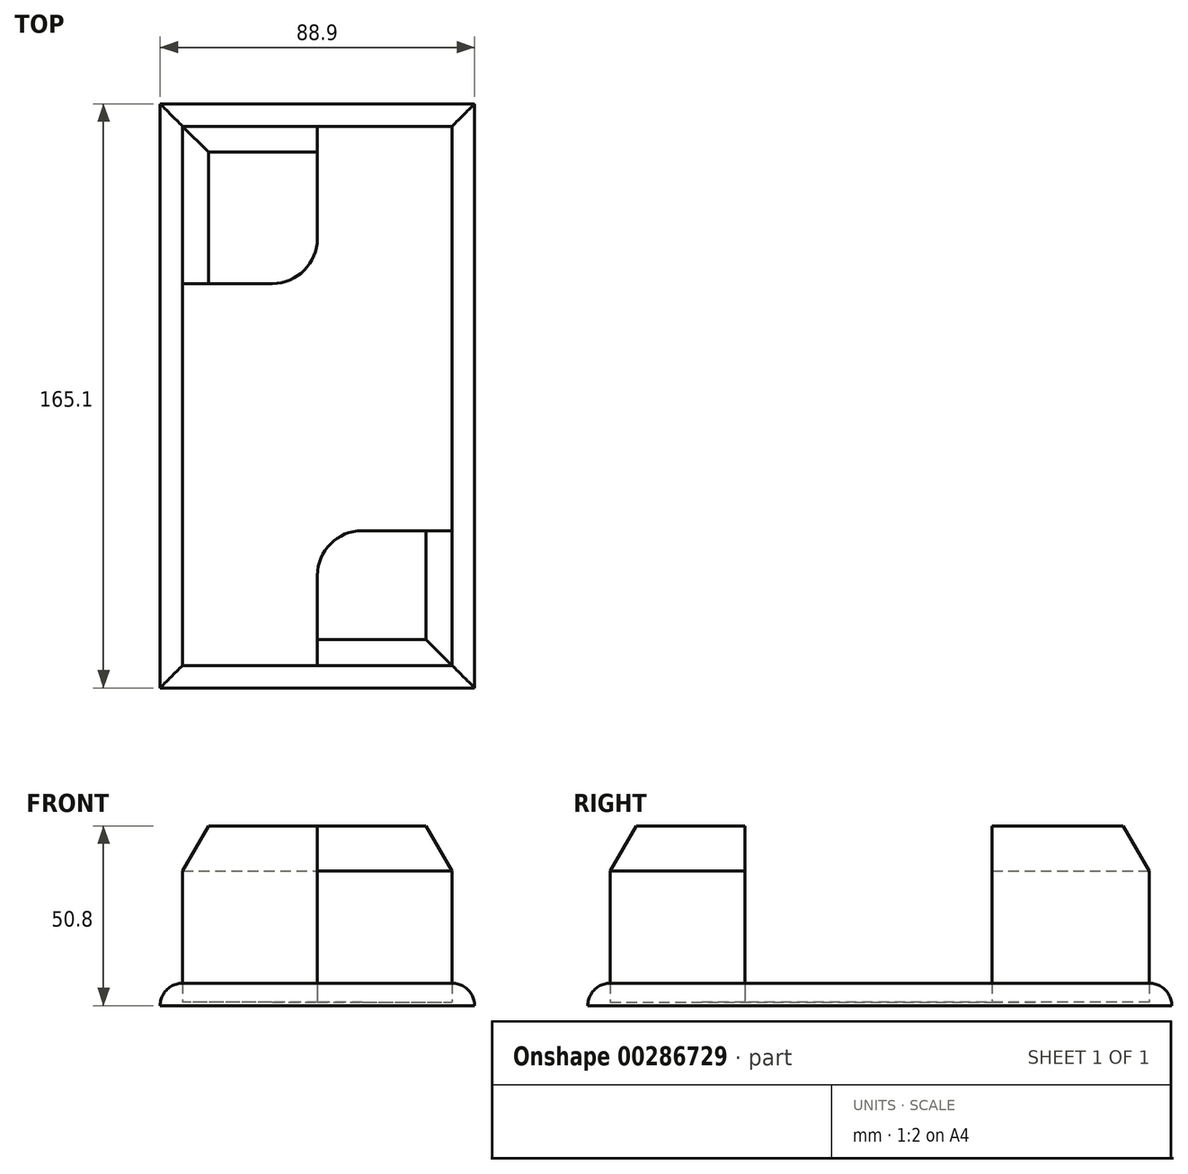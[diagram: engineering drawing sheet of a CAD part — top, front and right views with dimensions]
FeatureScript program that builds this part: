
annotation { "Feature Type Name" : "Feature", "Feature Type Description" : "" }
export const myFeature = defineFeature(function(context is Context, id is Id, definition is map)
    precondition{}
    {
        {
            var Q0;
            Q0=qCreatedBy(makeId("Top.planeOp"),FACE);
            var sketch = newSketch(context, id + "F0", { "sketchPlane" : qUnion([Q0])});
            skLineSegment(sketch, "E0", {"start": v(-50.93, 51.87) * mm, "end": v(25.27, 51.87) * mm});
            skLineSegment(sketch, "E1", {"start": v(25.27, 51.87) * mm, "end": v(25.27, -100.53) * mm});
            skLineSegment(sketch, "E2", {"start": v(25.27, -100.53) * mm, "end": v(-50.93, -100.53) * mm});
            skLineSegment(sketch, "E3", {"start": v(-50.93, -100.53) * mm, "end": v(-50.93, 51.87) * mm});
            skLineSegment(sketch, "E4.0", {"start": v(-57.28, 58.22) * mm, "end": v(31.62, 58.22) * mm});
            skLineSegment(sketch, "E4.1", {"start": v(-57.28, -106.88) * mm, "end": v(-57.28, 58.22) * mm});
            skLineSegment(sketch, "E4.2", {"start": v(31.62, -106.88) * mm, "end": v(-57.28, -106.88) * mm});
            skLineSegment(sketch, "E4.3", {"start": v(31.62, 58.22) * mm, "end": v(31.62, -106.88) * mm});
            skLineSegment(sketch, "E5", {"start": v(-12.83, 51.87) * mm, "end": v(-12.83, 20.12) * mm});
            skLineSegment(sketch, "E6", {"start": v(-25.53, 7.42) * mm, "end": v(-50.93, 7.42) * mm});
            skArc(sketch, "E7.filletArc", {"start": v(-25.53, 7.42) * mm, "mid": v(-16.55, 11.14) * mm, "end": v(-12.83, 20.12) * mm});
            skLineSegment(sketch, "E8", {"start": v(-12.83, -100.53) * mm, "end": v(-12.83, -75.13) * mm});
            skLineSegment(sketch, "E9", {"start": v(-0.13, -62.43) * mm, "end": v(25.27, -62.43) * mm});
            skArc(sketch, "E10.filletArc", {"start": v(-0.13, -62.43) * mm, "mid": v(-9.11, -66.15) * mm, "end": v(-12.83, -75.13) * mm});
            skSolve(sketch);
        }
        {
            var Q0;
            {var subQ9=sQuery(id+"F0.wireOp",EDGE,"E5");Q0=makeQuery(id+"F0.imprint","IMPRINT",FACE,{"disambiguationData":[TD([[makeQuery(id+"F0.imprint","IMPRINT",EDGE,{"derivedFrom":subQ9}),1.0]])]});}
            extrude(context, id + "F1", {"entities" : qUnion([Q0]), "depth" : mm});
        }
        {
            var Q0;
            {var subQ1=sQuery(id+"F0.wireOp",EDGE,"E8");Q0=makeQuery(id+"F0.imprint","IMPRINT",FACE,{"disambiguationData":[TD([[makeQuery(id+"F0.imprint","IMPRINT",EDGE,{"derivedFrom":subQ1}),-1.0]])]});}
            var Q1;
            {var subQ1=sQuery(id+"F0.wireOp",EDGE,"E5");Q1=makeQuery(id+"F0.imprint","IMPRINT",FACE,{"disambiguationData":[TD([[makeQuery(id+"F0.imprint","IMPRINT",EDGE,{"derivedFrom":subQ1}),-1.0]])]});}
            extrude(context, id + "F2", {"entities" : qUnion([Q0, Q1]), "operationType" : NewBodyOperationType.ADD, "depth" : 50.8 * mm});
        }
        {
            var Q0;
            Q0=makeQuery(id+"F0.imprint","IMPRINT",FACE,{"disambiguationData":[TD([[makeQuery(id+"F0.imprint","IMPRINT",EDGE,{"derivedFrom":sQuery(id+"F0.wireOp",EDGE,"E4.0")}),-1.0]])]});
            extrude(context, id + "F3", {"entities" : qUnion([Q0]), "operationType" : NewBodyOperationType.ADD, "depth" : 6.35 * mm});
        }
        {
            var Q0;
            Q0=makeQuery(id+"F3.opExtrude","CAP_EDGE",EDGE,{"disambiguationData":[OSD([sQuery(id+"F0.wireOp",EDGE,"E4.1")])],"isStart":false});
            var Q1;
            Q1=makeQuery(id+"F3.opExtrude","CAP_EDGE",EDGE,{"disambiguationData":[OSD([sQuery(id+"F0.wireOp",EDGE,"E4.2")])],"isStart":false});
            var Q2;
            Q2=makeQuery(id+"F3.opExtrude","CAP_EDGE",EDGE,{"disambiguationData":[OSD([sQuery(id+"F0.wireOp",EDGE,"E4.3")])],"isStart":false});
            var Q3;
            Q3=makeQuery(id+"F3.opExtrude","CAP_EDGE",EDGE,{"disambiguationData":[OSD([sQuery(id+"F0.wireOp",EDGE,"E4.0")])],"isStart":false});
            fillet(context, id + "F4", {"entities" : qUnion([Q0, Q1, Q2, Q3]), "radius" : 6.35 * mm, "tangentPropagation" : true, "allowEdgeOverflow" : false});
        }
        {
            var Q0;
            Q0=makeQuery(id+"F1.opExtrude","CAP_EDGE",EDGE,{"disambiguationData":[OSD([sQuery(id+"F0.wireOp",EDGE,"E1")])],"isStart":false});
            var Q1;
            Q1=makeQuery(id+"F1.opExtrude","CAP_EDGE",EDGE,{"disambiguationData":[OSD([sQuery(id+"F0.wireOp",EDGE,"E0")])],"isStart":false});
            var Q2;
            Q2=makeQuery(id+"F2.opExtrude","CAP_EDGE",EDGE,{"disambiguationData":[OSD([sQuery(id+"F0.wireOp",EDGE,"E0")])],"isStart":false});
            var Q3;
            Q3=makeQuery(id+"F2.opExtrude","CAP_EDGE",EDGE,{"disambiguationData":[OSD([sQuery(id+"F0.wireOp",EDGE,"E3")])],"isStart":false});
            var Q4;
            Q4=makeQuery(id+"F1.opExtrude","CAP_EDGE",EDGE,{"disambiguationData":[OSD([sQuery(id+"F0.wireOp",EDGE,"E3")])],"isStart":false});
            var Q5;
            Q5=makeQuery(id+"F2.opExtrude","CAP_EDGE",EDGE,{"disambiguationData":[OSD([sQuery(id+"F0.wireOp",EDGE,"E1")])],"isStart":false});
            var Q6;
            Q6=makeQuery(id+"F1.opExtrude","CAP_EDGE",EDGE,{"disambiguationData":[OSD([sQuery(id+"F0.wireOp",EDGE,"E2")])],"isStart":false});
            var Q7;
            Q7=makeQuery(id+"F2.opExtrude","CAP_EDGE",EDGE,{"disambiguationData":[OSD([sQuery(id+"F0.wireOp",EDGE,"E2")])],"isStart":false});
            chamfer(context, id + "F5", {"entities" : qUnion([Q0, Q1, Q2, Q3, Q4, Q5, Q6, Q7]), "chamferType" : ChamferType.OFFSET_ANGLE, "width" : 12.7 * mm, "oppositeDirection" : false, "angle" : 30 * degree, "tangentPropagation" : true});
        }
    });
